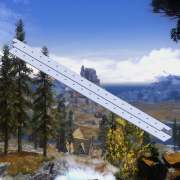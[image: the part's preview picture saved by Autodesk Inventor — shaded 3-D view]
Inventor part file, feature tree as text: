
AUTODESK INVENTOR PART (.ipt)
format: ipt  version: 2015 SP1 (Build 190203100, 203)  size: 421,376 bytes
history: native  units: in
note: dims shown in document units (in); Inventor stores cm internally (conversion verified against a paired STEP export)
features: other x2, extrude x2, sketch x2, plane x1, imported_body x1
ambient origin geometry x8: Origin, YZ Plane, XZ Plane, XY Plane, X Axis, Y Axis, Z Axis, Center Point
bodies: Body1 (feature_tree)
feature tree (8):
  other  "Break-Corner1"
  other  "VersaFrame 1 x 1 x 1 x 0.090 C-Channel (59 length)(217-4107)1"
  plane  "Work Plane1"
  extrude  "Extrusion1"  Depth=1.0in TaperAngle=0.0deg
  extrude  "Extrusion2"  [1 undecoded]
  imported_body  "Base1"
  sketch  "Sketch1"  dims[d0=19.0in d1=1.0in d2=0.0in]
  sketch  "Sketch2"  dims[d3=0.5in d4=0.0in]
note: 1 required parameter value undecoded (feature->parameter linkage not recoverable at this tier; creation-order binding heuristic only, values carry confidence <= 0.55)
